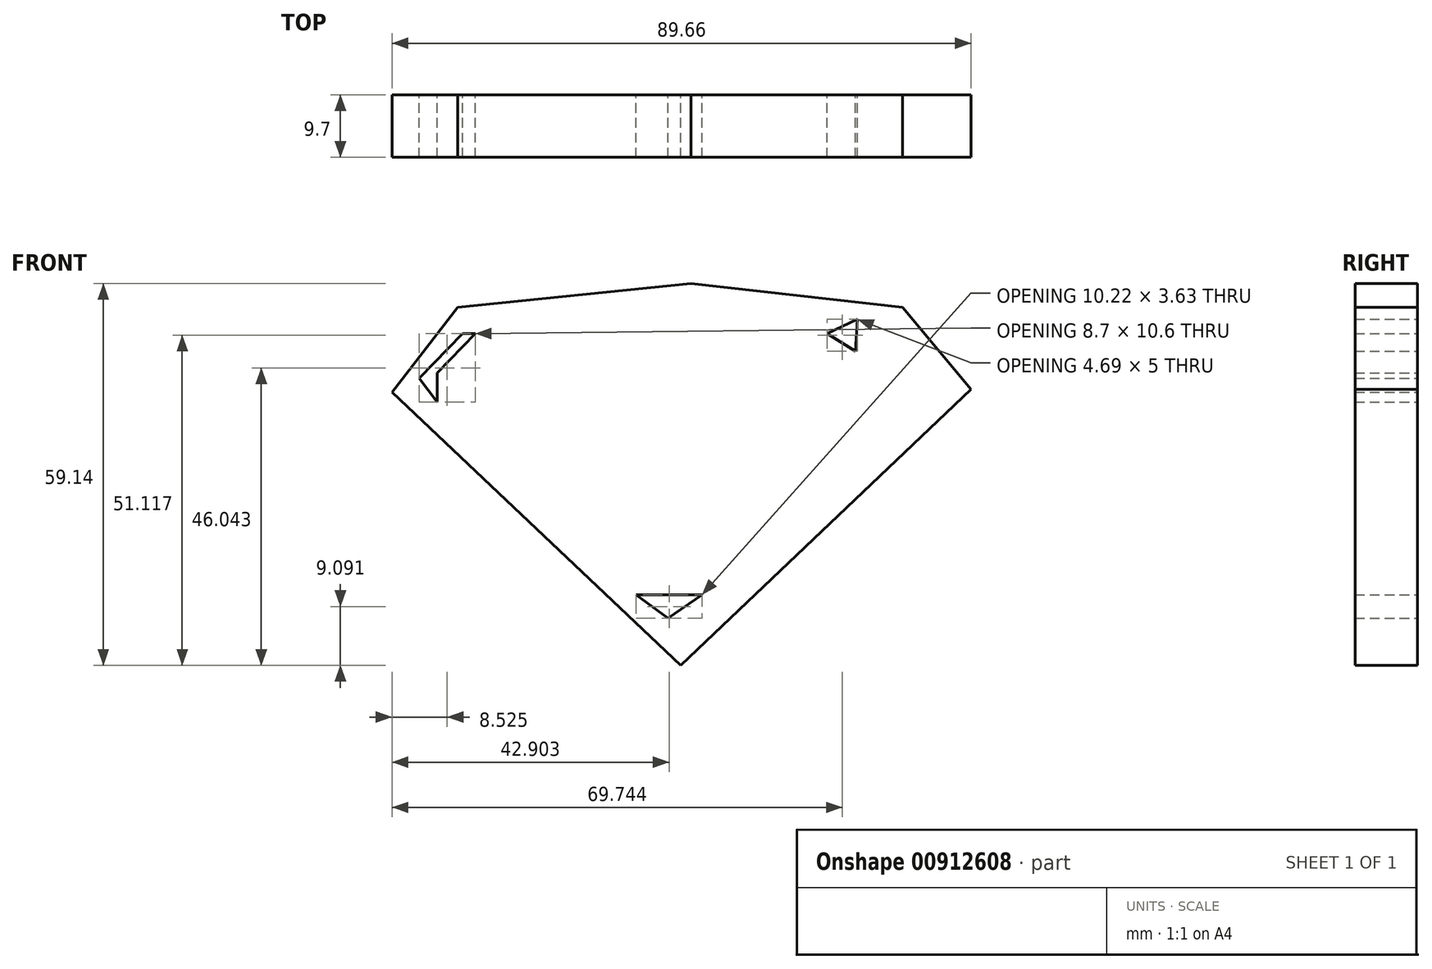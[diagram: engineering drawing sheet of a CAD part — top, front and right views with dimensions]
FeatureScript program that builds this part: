
annotation { "Feature Type Name" : "Feature", "Feature Type Description" : "" }
export const myFeature = defineFeature(function(context is Context, id is Id, definition is map)
    precondition{}
    {
        {
            var Q0;
            Q0=qCreatedBy(makeId("Front.planeOp"),FACE);
            var sketch = newSketch(context, id + "F0", { "sketchPlane" : qUnion([Q0])});
            skLineSegment(sketch, "E0", {"start": v(-2.12, -32.49) * mm, "end": v(-46.8, 9.77) * mm});
            skLineSegment(sketch, "E1", {"start": v(-46.8, 9.77) * mm, "end": v(-36.65, 22.94) * mm});
            skLineSegment(sketch, "E2", {"start": v(-36.65, 22.94) * mm, "end": v(-0.52, 26.65) * mm});
            skLineSegment(sketch, "E3", {"start": v(-0.52, 26.65) * mm, "end": v(32.26, 22.94) * mm});
            skLineSegment(sketch, "E4", {"start": v(32.26, 22.94) * mm, "end": v(42.86, 10.22) * mm});
            skLineSegment(sketch, "E5", {"start": v(42.86, 10.22) * mm, "end": v(-2.12, -32.49) * mm});
            skPoint(sketch, "E6.endSnap0", {"position": v(27.76, 10.02) * mm});
            skLineSegment(sketch, "E7", {"start": v(28.47, 17.8) * mm, "end": v(28.47, 10.22) * mm});
            skLineSegment(sketch, "E8", {"start": v(28.47, 10.22) * mm, "end": v(21.96, 10.22) * mm});
            skFitSpline(sketch, "E9", {"points": [v(21.96, 10.22) * mm, v(17.87, 13.93) * mm, v(10.53, 18.32) * mm, v(1.67, 20.44) * mm, v(-8.7, 20.3) * mm, v(-16.58, 18.7) * mm, v(-18.17, 17.04) * mm, v(-18.32, 16.96) * mm, v(-18.78, 14.92) * mm, v(-18.78, 14.84) * mm, v(-17.19, 12.72) * mm, v(-17.26, 12.72) * mm, v(-12.04, 11.2) * mm, v(-1.29, 11.05) * mm, v(-1.21, 11.05) * mm, v(8.94, 9.54) * mm, v(9.01, 9.62) * mm, v(14.08, 7.42) * mm, v(14.08, 7.34) * mm, v(19.08, 4.7) * mm, v(21.96, -1.36) * mm], "startDerivative": vector(-58.23, 57.54) * mm, "endDerivative": vector(19.17, -95.11) * mm});
            skFitSpline(sketch, "E10", {"points": [v(8.04, -11.56) * mm, v(7.4, -12.28) * mm, v(5.8, -13.42) * mm, v(3.58, -14.48) * mm, v(0.62, -14.74) * mm, v(-4.26, -14.55) * mm, v(-9.52, -12.43) * mm, v(-14.22, -8.15) * mm], "startDerivative": vector(-7.17, -9.13) * mm, "endDerivative": vector(-22.72, 23.8) * mm});
            skLineSegment(sketch, "E11", {"start": v(-39.83, 8.25) * mm, "end": v(-39.83, 12.8) * mm});
            skLineSegment(sketch, "E12", {"start": v(-39.83, 12.8) * mm, "end": v(-33.92, 18.85) * mm});
            skLineSegment(sketch, "E13", {"start": v(-33.92, 18.85) * mm, "end": v(-35.9, 18.85) * mm});
            skLineSegment(sketch, "E14", {"start": v(-35.9, 18.85) * mm, "end": v(-42.63, 11.95) * mm});
            skLineSegment(sketch, "E15", {"start": v(-42.63, 11.95) * mm, "end": v(-39.83, 8.25) * mm});
            skLineSegment(sketch, "E16", {"start": v(24.99, 16.13) * mm, "end": v(20.6, 18.85) * mm});
            skLineSegment(sketch, "E17", {"start": v(20.6, 18.85) * mm, "end": v(25.3, 21.13) * mm});
            skLineSegment(sketch, "E18", {"start": v(25.3, 21.13) * mm, "end": v(24.99, 16.13) * mm});
            skLineSegment(sketch, "E19", {"start": v(-11.06, -20.07) * mm, "end": v(-4.09, -25.22) * mm});
            skLineSegment(sketch, "E20", {"start": v(-4.09, -25.22) * mm, "end": v(1.21, -21.58) * mm});
            skLineSegment(sketch, "E21", {"start": v(1.21, -21.58) * mm, "end": v(-9, -21.58) * mm});
            skSolve(sketch);
        }
        {
            var Q0;
            Q0=makeQuery(id+"F0.imprint","IMPRINT",FACE,{"disambiguationData":[TD([[makeQuery(id+"F0.imprint","IMPRINT",EDGE,{"derivedFrom":sQuery(id+"F0.wireOp",EDGE,"E0")}),-1.0]])]});
            extrude(context, id + "F1", {"entities" : qUnion([Q0]), "endBound" : BoundingType.SYMMETRIC, "depth" : 9.7 * mm, "offsetDistance" : 25 * mm});
        }
    });
